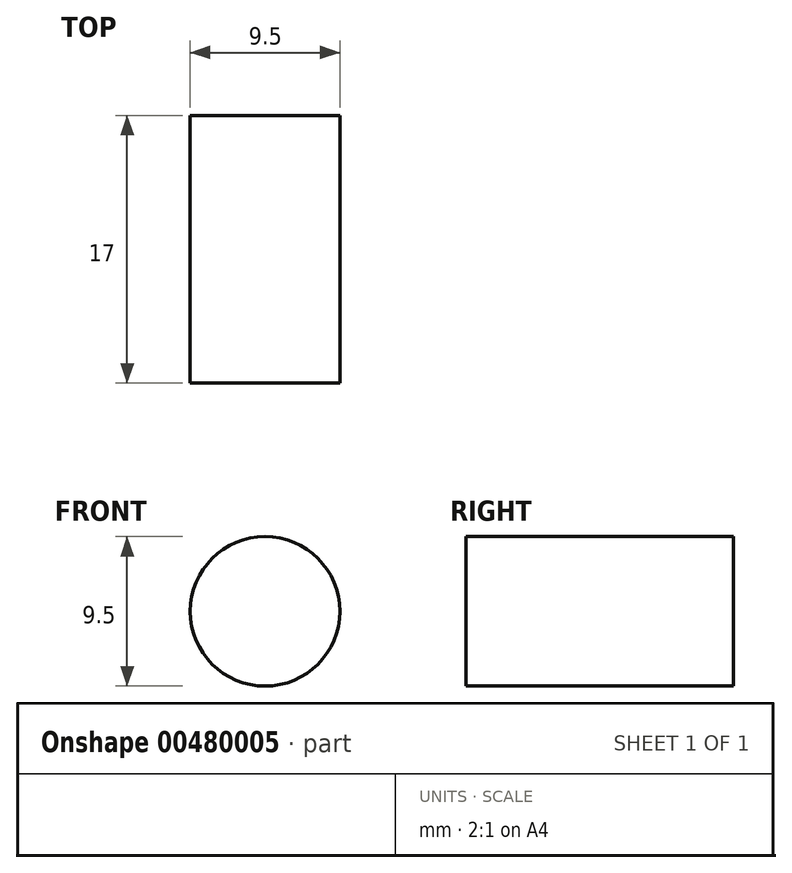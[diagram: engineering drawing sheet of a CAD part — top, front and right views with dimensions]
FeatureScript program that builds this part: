
annotation { "Feature Type Name" : "Feature", "Feature Type Description" : "" }
export const myFeature = defineFeature(function(context is Context, id is Id, definition is map)
    precondition{}
    {
        {
            var Q0;
            Q0=qCreatedBy(makeId("Front.planeOp"),FACE);
            var sketch = newSketch(context, id + "F0", { "sketchPlane" : qUnion([Q0])});
            skCircle(sketch, "E0", {"center": v(0, 0) * mm, "radius": 4.75 * mm});
            skSolve(sketch);
        }
        {
            var Q0;
            Q0=makeQuery(id+"F0.imprint","IMPRINT",FACE,{"disambiguationData":[TD([[makeQuery(id+"F0.imprint","IMPRINT",EDGE,{"derivedFrom":sQuery(id+"F0.wireOp",EDGE,"E0")}),1.0]])]});
            extrude(context, id + "F1", {"entities" : qUnion([Q0]), "depth" : 17 * mm});
        }
    });
